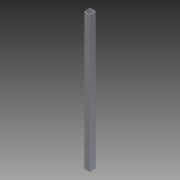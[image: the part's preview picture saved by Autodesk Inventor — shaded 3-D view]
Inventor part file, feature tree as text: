
AUTODESK INVENTOR PART (.ipt)
format: ipt  version: 2013 (Build 170138000, 138)  size: 88,576 bytes
history: native  units: in
note: dims shown in document units (in); Inventor stores cm internally (conversion verified against a paired STEP export)
features: extrude x2, sketch x2
ambient origin geometry x8: Origin, YZ Plane, XZ Plane, XY Plane, X Axis, Y Axis, Z Axis, Center Point
bodies: Solid1 (feature_tree)
feature tree (4):
  extrude  "Extrusion1"  Depth=1.0in
  extrude  "Extrusion2"  Depth=30.0in TaperAngle=0.0deg
  sketch  "Sketch1"  dims[d0=1.0in d2=1.0in]
  sketch  "Sketch2"  dims[d3=0.0625in d4=30.0in d5=0.0in d6=23.5in d8=23.585in d9=30.0in d10=0.0in]
